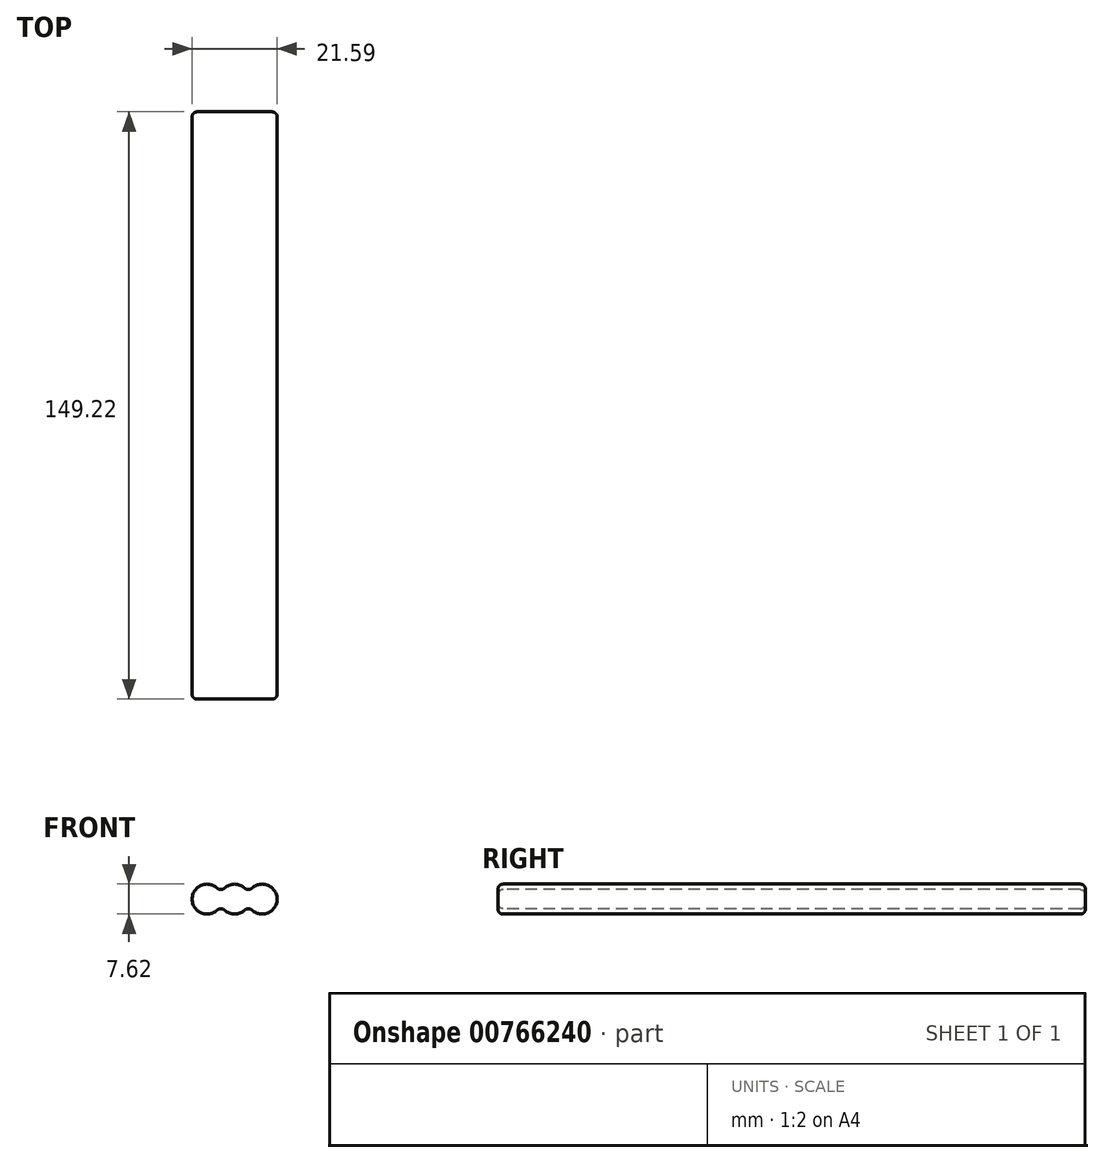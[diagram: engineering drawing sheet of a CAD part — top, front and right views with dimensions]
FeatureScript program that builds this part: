
annotation { "Feature Type Name" : "Feature", "Feature Type Description" : "" }
export const myFeature = defineFeature(function(context is Context, id is Id, definition is map)
    precondition{}
    {
        {
            var Q0;
            Q0=qCreatedBy(makeId("Front.planeOp"),FACE);
            var sketch = newSketch(context, id + "F0", { "sketchPlane" : qUnion([Q0])});
            skLineSegment(sketch, "E0", {"start": v(-6.99, 0) * mm, "end": v(6.99, 0) * mm, "construction": true});
            skArc(sketch, "E1", {"start": v(3.5, 1.52) * mm, "mid": v(0, 3.8) * mm, "end": v(-3.5, 1.52) * mm});
            skArc(sketch, "E2", {"start": v(3.5, -1.52) * mm, "mid": v(10.8, 0) * mm, "end": v(3.5, 1.52) * mm});
            skArc(sketch, "E3", {"start": v(-3.5, 1.52) * mm, "mid": v(-10.8, 0) * mm, "end": v(-3.5, -1.52) * mm});
            skArc(sketch, "E4.trimOffspring", {"start": v(-3.5, -1.52) * mm, "mid": v(0, -3.8) * mm, "end": v(3.5, -1.52) * mm});
            skSolve(sketch);
        }
        {
            var Q0;
            Q0=qSketchRegion(id+"F0",true);
            extrude(context, id + "F1", {"entities" : qUnion([Q0]), "endBound" : BoundingType.SYMMETRIC, "depth" : 149.22 * mm, "offsetDistance" : 25.4 * mm});
        }
        {
            var Q0;
            Q0=makeQuery(id+"F1.opExtrude","CAP_FACE",FACE,{"disambiguationData":[OSD([sQuery(id+"F0.wireOp",EDGE,"E1"),sQuery(id+"F0.wireOp",EDGE,"E2"),sQuery(id+"F0.wireOp",EDGE,"E3"),sQuery(id+"F0.wireOp",EDGE,"E4.trimOffspring")])],"isStart":true});
            var Q1;
            Q1=makeQuery(id+"F1.opExtrude","SWEPT_EDGE",EDGE,{"disambiguationData":[OSD([sQuery(id+"F0.wireOp",EDGE,"E1"),sQuery(id+"F0.wireOp",EDGE,"E2")])]});
            var Q2;
            Q2=makeQuery(id+"F1.opExtrude","SWEPT_EDGE",EDGE,{"disambiguationData":[OSD([sQuery(id+"F0.wireOp",EDGE,"E1"),sQuery(id+"F0.wireOp",EDGE,"E3")])]});
            var Q3;
            Q3=makeQuery(id+"F1.opExtrude","SWEPT_EDGE",EDGE,{"disambiguationData":[OSD([sQuery(id+"F0.wireOp",EDGE,"E2"),sQuery(id+"F0.wireOp",EDGE,"E4.trimOffspring")])]});
            var Q4;
            Q4=makeQuery(id+"F1.opExtrude","SWEPT_EDGE",EDGE,{"disambiguationData":[OSD([sQuery(id+"F0.wireOp",EDGE,"E3"),sQuery(id+"F0.wireOp",EDGE,"E4.trimOffspring")])]});
            var Q5;
            Q5=makeQuery(id+"F1.opExtrude","CAP_FACE",FACE,{"disambiguationData":[OSD([sQuery(id+"F0.wireOp",EDGE,"E1"),sQuery(id+"F0.wireOp",EDGE,"E2"),sQuery(id+"F0.wireOp",EDGE,"E3"),sQuery(id+"F0.wireOp",EDGE,"E4.trimOffspring")])],"isStart":false});
            fillet(context, id + "F2", {"entities" : qUnion([Q0, Q1, Q2, Q3, Q4, Q5]), "radius" : 1.27 * mm, "tangentPropagation" : true, "allowEdgeOverflow" : false});
        }
    });
